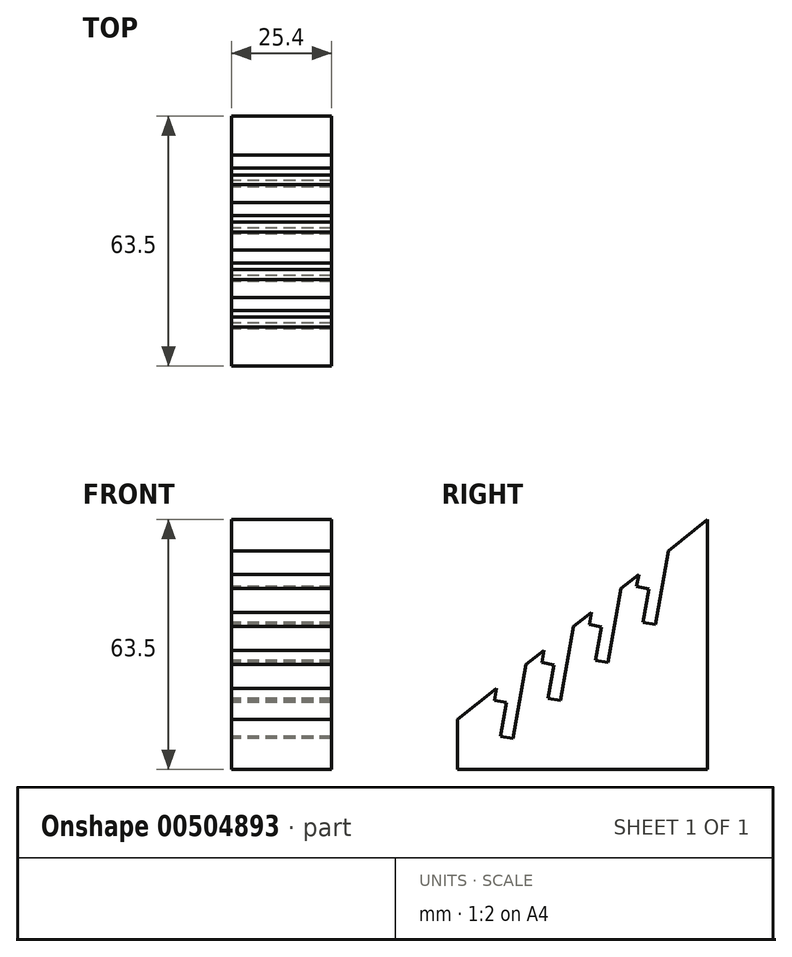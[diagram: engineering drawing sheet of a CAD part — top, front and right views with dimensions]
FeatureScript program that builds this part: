
annotation { "Feature Type Name" : "Feature", "Feature Type Description" : "" }
export const myFeature = defineFeature(function(context is Context, id is Id, definition is map)
    precondition{}
    {
        {
            var Q0;
            Q0=qCreatedBy(makeId("Right.planeOp"),FACE);
            var sketch = newSketch(context, id + "F0", { "sketchPlane" : qUnion([Q0])});
            skLineSegment(sketch, "E0", {"start": v(0, 0) * mm, "end": v(63.5, 0) * mm});
            skLineSegment(sketch, "E1", {"start": v(63.5, 0) * mm, "end": v(63.5, 63.5) * mm});
            skLineSegment(sketch, "E2", {"start": v(63.5, 63.5) * mm, "end": v(0, 12.7) * mm});
            skLineSegment(sketch, "E3", {"start": v(0, 12.7) * mm, "end": v(0, 0) * mm});
            skSolve(sketch);
        }
        {
            var Q0;
            Q0=qCreatedBy(makeId("Right.planeOp"),FACE);
            var sketch = newSketch(context, id + "F1", { "sketchPlane" : qUnion([Q0])});
            skLineSegment(sketch, "E4", {"start": v(9.92, 20.63) * mm, "end": v(9.37, 17.5) * mm});
            skLineSegment(sketch, "E5", {"start": v(9.37, 17.5) * mm, "end": v(12.42, 16.97) * mm});
            skLineSegment(sketch, "E6", {"start": v(14.12, 7.88) * mm, "end": v(17.42, 26.64) * mm});
            skLineSegment(sketch, "E7", {"start": v(9.92, 22.6) * mm, "end": v(9.92, 12.5) * mm, "construction": true});
            skLineSegment(sketch, "E8.0", {"start": v(63.5, 63.5) * mm, "end": v(0, 12.7) * mm, "construction": true});
            skLineSegment(sketch, "E9", {"start": v(12.42, 16.97) * mm, "end": v(10.91, 8.44) * mm});
            skLineSegment(sketch, "E10", {"start": v(10.91, 8.44) * mm, "end": v(14.12, 7.88) * mm});
            skLineSegment(sketch, "E11.1.0.0", {"start": v(21.97, 30.28) * mm, "end": v(21.42, 27.15) * mm});
            skLineSegment(sketch, "E11.1.0.1", {"start": v(21.42, 27.15) * mm, "end": v(24.47, 26.61) * mm});
            skLineSegment(sketch, "E11.1.0.2", {"start": v(26.17, 17.52) * mm, "end": v(29.48, 36.28) * mm});
            skLineSegment(sketch, "E11.1.0.3", {"start": v(24.47, 26.61) * mm, "end": v(22.97, 18.09) * mm});
            skLineSegment(sketch, "E11.1.0.4", {"start": v(22.97, 18.09) * mm, "end": v(26.17, 17.52) * mm});
            skLineSegment(sketch, "E11.2.0.0", {"start": v(34.02, 39.92) * mm, "end": v(33.47, 36.8) * mm});
            skLineSegment(sketch, "E11.2.0.1", {"start": v(33.47, 36.8) * mm, "end": v(36.52, 36.25) * mm});
            skLineSegment(sketch, "E11.2.0.2", {"start": v(38.22, 27.16) * mm, "end": v(41.53, 45.92) * mm});
            skLineSegment(sketch, "E11.2.0.3", {"start": v(36.52, 36.25) * mm, "end": v(35.02, 27.73) * mm});
            skLineSegment(sketch, "E11.2.0.4", {"start": v(35.02, 27.73) * mm, "end": v(38.22, 27.16) * mm});
            skLineSegment(sketch, "E11.3.0.0", {"start": v(46.08, 49.56) * mm, "end": v(45.52, 46.43) * mm});
            skLineSegment(sketch, "E11.3.0.1", {"start": v(45.52, 46.43) * mm, "end": v(48.58, 45.9) * mm});
            skLineSegment(sketch, "E11.3.0.2", {"start": v(50.27, 36.8) * mm, "end": v(53.58, 55.57) * mm});
            skLineSegment(sketch, "E11.3.0.3", {"start": v(48.58, 45.9) * mm, "end": v(47.07, 37.37) * mm});
            skLineSegment(sketch, "E11.3.0.4", {"start": v(47.07, 37.37) * mm, "end": v(50.27, 36.8) * mm});
            skLineSegment(sketch, "E11.direction1", {"start": v(9.37, 17.5) * mm, "end": v(21.42, 27.15) * mm, "construction": true});
            skLineSegment(sketch, "E12", {"start": v(9.92, 20.63) * mm, "end": v(17.42, 26.64) * mm});
            skLineSegment(sketch, "E13", {"start": v(21.97, 30.28) * mm, "end": v(29.48, 36.28) * mm});
            skLineSegment(sketch, "E14", {"start": v(34.02, 39.92) * mm, "end": v(41.53, 45.92) * mm});
            skLineSegment(sketch, "E15", {"start": v(46.08, 49.56) * mm, "end": v(53.58, 55.57) * mm});
            skSolve(sketch);
        }
        {
            var Q0;
            Q0 = qSketchRegion(id + "F0", true);
            extrude(context, id + "F2", {"entities" : qUnion([Q0]), "depth" : 25.4 * mm});
        }
        {
            var Q0;
            Q0 = qSketchRegion(id + "F1", true);
            extrude(context, id + "F3", {"entities" : qUnion([Q0]), "operationType" : NewBodyOperationType.REMOVE, "depth" : 25.4 * mm});
        }
    });
